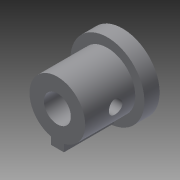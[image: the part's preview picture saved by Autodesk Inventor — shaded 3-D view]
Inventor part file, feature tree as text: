
AUTODESK INVENTOR PART (.ipt)
format: ipt  version: 2015 (Build 190159000, 159)  size: 142,336 bytes
history: native  units: in
note: dims shown in document units (in); Inventor stores cm internally (conversion verified against a paired STEP export)
features: sketch x3, extrude x3, revolve x1, plane x1
ambient origin geometry x8: Origin, YZ Plane, XZ Plane, XY Plane, X Axis, Y Axis, Z Axis, Center Point
bodies: Solid1 (feature_tree)
feature tree (8):
  sketch  "Sketch1"  dims[d0=0.2756in d1=0.122in]
  revolve  "Revolution1"  [1 undecoded]
  plane  "Work Plane1"
  sketch  "Sketch2"  dims[d2=0.252in d3=0.122in]
  extrude  "Extrusion2"  Depth=0.252in
  extrude  "Extrusion3"  Depth=0.1575in
  extrude  "Extrusion4"  Depth=0.4528in
  sketch  "Sketch3"  dims[d4=0.315in d5=0.1575in d6=0.3346in d7=0.1378in d8=90.0deg d11=0.2756in d12=0.122in d13=0.315in d14=1.1811in d15=0.0in d16=0.1181in d17=0.0in d18=0.0591in d19=0.0591in d20=0.0591in d21=0.0591in d22=0.0591in d23=0.0591in d24=0.4528in d25=0.0in]
note: 1 required parameter value undecoded (feature->parameter linkage not recoverable at this tier; creation-order binding heuristic only, values carry confidence <= 0.55)
